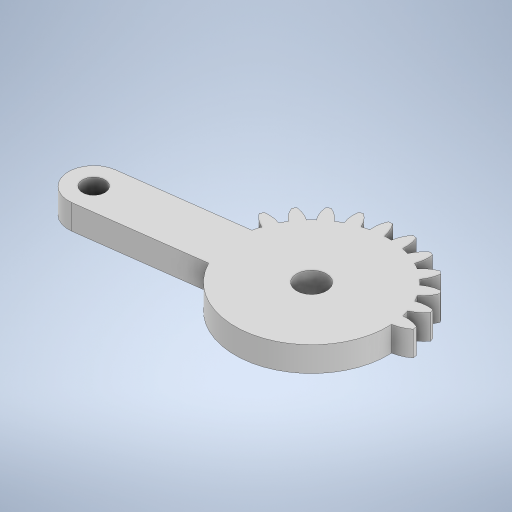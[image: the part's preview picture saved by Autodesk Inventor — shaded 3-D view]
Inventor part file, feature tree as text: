
AUTODESK INVENTOR PART (.ipt)
format: ipt  version: 2024.1 (Build 281209000, 209)  size: 344,576 bytes
history: native  units: in
note: dims shown in document units (in); Inventor stores cm internally (conversion verified against a paired STEP export)
features: extrude x1, direct_edit x1, sketch x1, other x1
ambient origin geometry x8: Origin, YZ Plane, XZ Plane, XY Plane, X Axis, Y Axis, Z Axis, Center Point
bodies: Solid1 (feature_tree)
feature tree (4):
  extrude  "Extrusion1"  Depth=0.3937in
  direct_edit  "Direct Edit2"
  sketch  "Sketch1"  dims[d1=3.5433in d2=24.2126in d3=4.7244in d10=4.3307in d12=150.0deg d14=3.937in d15=0.0in d19=0.0394in d20=0.3937in d21=0.3937in]
  other  "Scale2"
